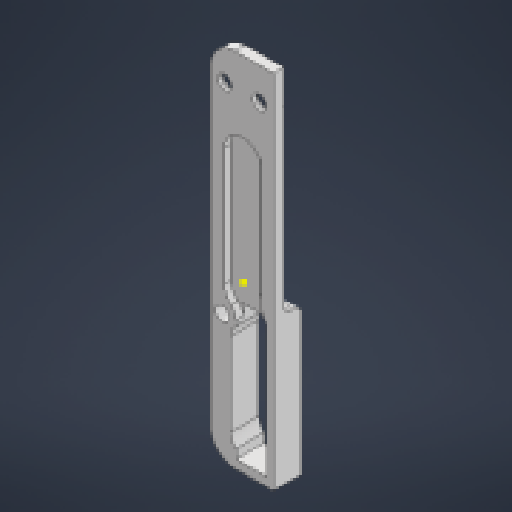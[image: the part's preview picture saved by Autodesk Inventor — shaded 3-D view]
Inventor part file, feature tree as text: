
AUTODESK INVENTOR PART (.ipt)
format: ipt  version: 2025 (Build 290162000, 162)  size: 305,152 bytes
history: native  units: mm
features: reference x12, sketch x10, extrude x7, other x5, fillet x2, chamfer x1
ambient origin geometry x8: Origin, YZ Plane, XZ Plane, XY Plane, X Axis, Y Axis, Z Axis, Center Point
bodies: 实体1 (feature_tree)
feature tree (37):
  sketch  "草图1"  dims[d0=4.0mm d1=0.0mm d2=4.0mm d3=0.0mm]
  extrude  "拉伸1"  Depth=4.0mm TaperAngle=0.0deg
  sketch  "草图3"  dims[d7=1.5mm d8=33.0mm d9=0.0mm]
  extrude  "拉伸2"  Depth=1.0mm
  extrude  "拉伸3"  Depth=1.5mm TaperAngle=0.0deg
  extrude  "拉伸4"  Depth=1.0mm
  fillet  "圆角1"  Radius=1.0mm
  extrude  "拉伸5"  Depth=1.0mm TaperAngle=0.0deg
  fillet  "圆角2"  Radius=2.0mm
  extrude  "拉伸6"  Depth=2.0mm
  sketch  "草图9"
  extrude  "拉伸7"  Depth=2.0mm
  chamfer  "倒角1"  Distance=9.5mm
  sketch  "草图2"  dims[d4=2.0mm d5=0.0mm d6=1.0mm]
  reference  "参考1"
  reference  "参考2"
  sketch  "草图4"  dims[d10=1.0mm d11=1.0mm d12=1.0mm d13=0.0mm]
  reference  "参考3"
  reference  "参考4"
  sketch  "草图5"  dims[d14=2.0mm d15=1.0mm d16=0.0mm d17=2.0mm]
  reference  "参考5"
  sketch  "草图6"  dims[d18=2.0mm d19=2.0mm]
  reference  "参考6"
  sketch  "草图7"  dims[d20=2.0mm d21=2.0mm d22=9.5mm d23=0.0mm]
  reference  "参考7"
  reference  "参考8"
  reference  "参考9"
  reference  "参考10"
  reference  "参考11"
  reference  "参考12"
  sketch  "草图8"  dims[d24=1.0mm d25=2.0mm d26=45.0deg]
  sketch  "草图10"
  parser-record x1  (decoder bookkeeping rows leaked as tree rows — omitted from the tree; the rows remain in map.json)
  other  "dlc.iam"
  other  "指纹dlc:1"
  other  "指纹识别:1"
  other  "音量接口:1"
note: 1 file-system path scrubbed to <path> (originals preserved in map.json)
